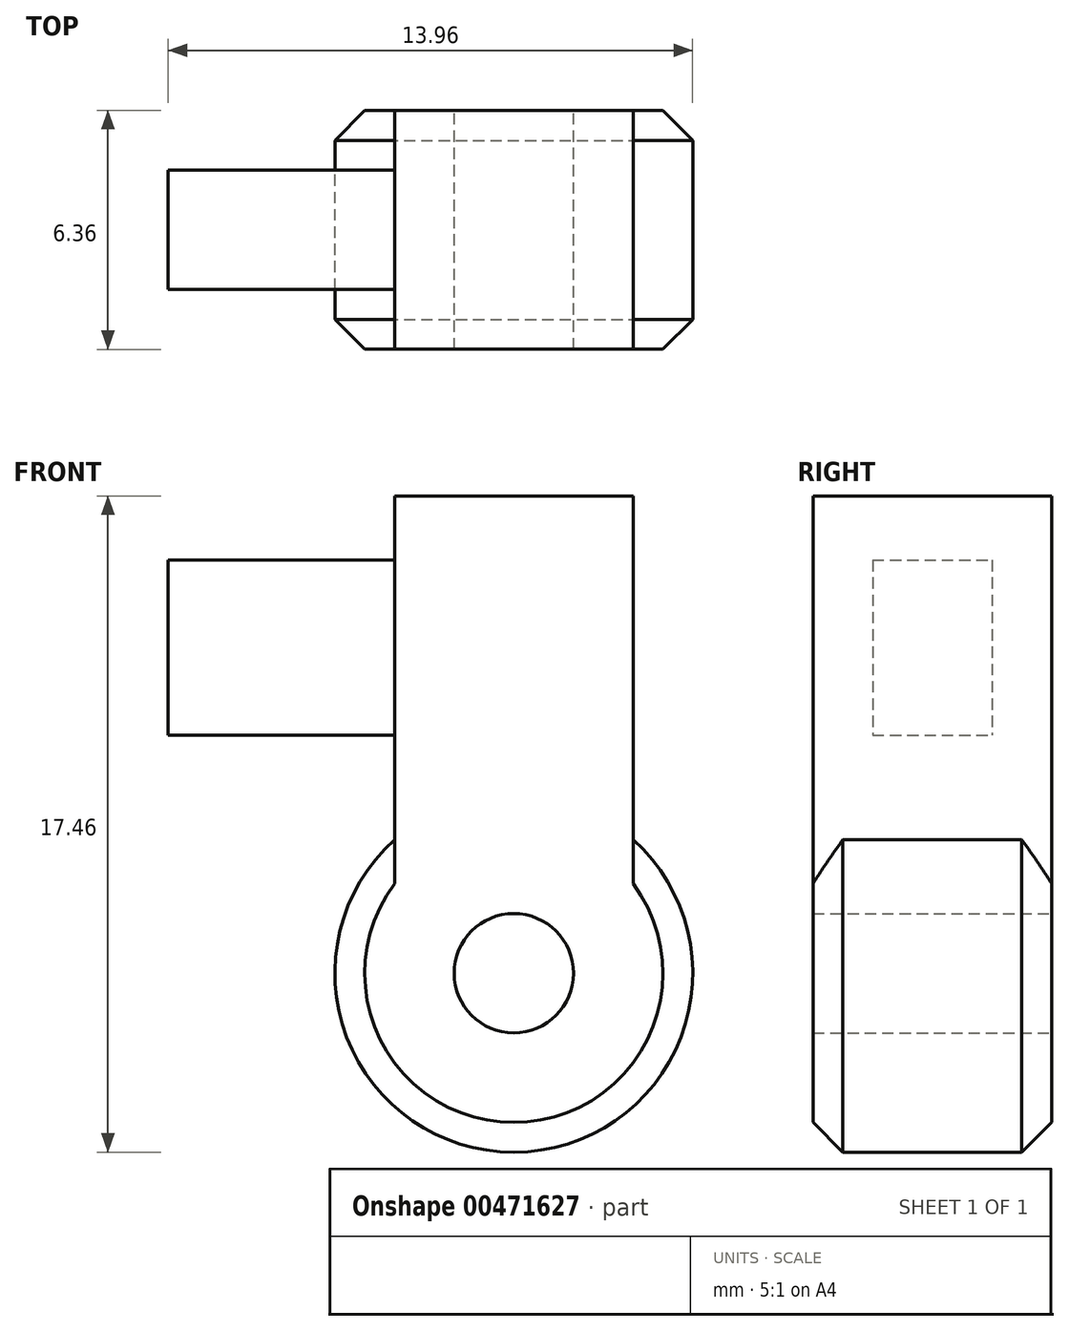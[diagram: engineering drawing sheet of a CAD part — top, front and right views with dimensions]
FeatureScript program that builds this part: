
annotation { "Feature Type Name" : "Feature", "Feature Type Description" : "" }
export const myFeature = defineFeature(function(context is Context, id is Id, definition is map)
    precondition{}
    {
        {
            var Q0;
            Q0=qCreatedBy(makeId("Front.planeOp"),FACE);
            var sketch = newSketch(context, id + "F0", { "sketchPlane" : qUnion([Q0])});
            skLineSegment(sketch, "E0.bottom", {"start": v(77.53, -76.45) * mm, "end": v(-77.53, -76.45) * mm});
            skLineSegment(sketch, "E0.top", {"start": v(77.53, 76.45) * mm, "end": v(-77.53, 76.45) * mm});
            skLineSegment(sketch, "E0.left", {"start": v(77.53, -76.45) * mm, "end": v(77.53, 76.45) * mm});
            skLineSegment(sketch, "E0.right", {"start": v(-77.53, -76.45) * mm, "end": v(-77.53, 76.45) * mm});
            skPoint(sketch, "E0.middle", {"position": v(0, 0) * mm});
            skSolve(sketch);
        }
        {
            var Q0;
            Q0=makeQuery(id+"F0.imprint","IMPRINT",FACE,{"disambiguationData":[TD([[makeQuery(id+"F0.imprint","IMPRINT",EDGE,{"derivedFrom":sQuery(id+"F0.wireOp",EDGE,"E0.bottom")}),-1.0]])]});
            cPlane(context, id + "F1", {"entities" : qUnion([Q0]), "cplaneType" : CPlaneType.OFFSET, "offset" : 25.4 * mm, "width" : 152.4 * mm, "height" : 152.4 * mm});
        }
        {
            var Q0;
            Q0=qCreatedBy(id+"F1.planeOp",FACE);
            var sketch = newSketch(context, id + "F2", { "sketchPlane" : qUnion([Q0])});
            skCircle(sketch, "E1", {"center": v(0, 0) * mm, "radius": 1.59 * mm});
            skCircle(sketch, "E2.0", {"center": v(0, 0) * mm, "radius": 4.76 * mm});
            skSolve(sketch);
        }
        {
            var Q0;
            Q0=qCreatedBy(id+"F1.planeOp",FACE);
            var sketch = newSketch(context, id + "F3", { "sketchPlane" : qUnion([Q0])});
            skLineSegment(sketch, "E3.bottom", {"start": v(3.18, 12.7) * mm, "end": v(-3.18, 12.7) * mm});
            skLineSegment(sketch, "E3.left", {"start": v(3.18, 12.7) * mm, "end": v(3.18, 0) * mm});
            skLineSegment(sketch, "E3.right", {"start": v(-3.18, 12.7) * mm, "end": v(-3.18, 0) * mm});
            skPoint(sketch, "E3.middle", {"position": v(0, 0) * mm});
            skPoint(sketch, "E4", {"position": v(3.18, 0) * mm});
            skPoint(sketch, "E5", {"position": v(-3.18, 0) * mm});
            skLineSegment(sketch, "E6", {"start": v(3.18, 0) * mm, "end": v(-3.18, 0) * mm});
            skCircle(sketch, "E7", {"center": v(0, 0) * mm, "radius": 1.59 * mm});
            skSolve(sketch);
        }
        {
            var Q0;
            Q0=qCreatedBy(id+"F1.planeOp",FACE);
            var sketch = newSketch(context, id + "F4", { "sketchPlane" : qUnion([Q0])});
            skLineSegment(sketch, "E8.bottom", {"start": v(-1.96, 6.34) * mm, "end": v(-9.2, 6.34) * mm});
            skLineSegment(sketch, "E8.top", {"start": v(-1.96, 11) * mm, "end": v(-9.2, 11) * mm});
            skLineSegment(sketch, "E8.left", {"start": v(-1.96, 6.34) * mm, "end": v(-1.96, 11) * mm});
            skLineSegment(sketch, "E8.right", {"start": v(-9.2, 6.34) * mm, "end": v(-9.2, 11) * mm});
            skSolve(sketch);
        }
        {
            var Q0;
            Q0=makeQuery(id+"F2.imprint","IMPRINT",FACE,{"disambiguationData":[TD([[makeQuery(id+"F2.imprint","IMPRINT",EDGE,{"derivedFrom":sQuery(id+"F2.wireOp",EDGE,"E1")}),-1.0]])]});
            extrude(context, id + "F5", {"entities" : qUnion([Q0]), "depth" : 6.35 * mm, "symmetric" : true});
        }
        {
            var Q0;
            Q0=makeQuery(id+"F3.imprint","IMPRINT",FACE,{"disambiguationData":[TD([[makeQuery(id+"F3.imprint","IMPRINT",EDGE,{"derivedFrom":sQuery(id+"F3.wireOp",EDGE,"E3.bottom")}),1.0]])]});
            extrude(context, id + "F6", {"entities" : qUnion([Q0]), "operationType" : NewBodyOperationType.ADD, "depth" : 6.35 * mm, "symmetric" : true});
        }
        {
            var Q0;
            Q0=makeQuery(id+"F4.imprint","IMPRINT",FACE,{"disambiguationData":[TD([[makeQuery(id+"F4.imprint","IMPRINT",EDGE,{"derivedFrom":sQuery(id+"F4.wireOp",EDGE,"E8.bottom")}),-1.0]])]});
            extrude(context, id + "F7", {"entities" : qUnion([Q0]), "operationType" : NewBodyOperationType.ADD, "depth" : 3.17 * mm, "symmetric" : true});
        }
        {
            var Q0;
            Q0=makeQuery(id+"F5.opExtrude","CAP_EDGE",EDGE,{"disambiguationData":[OSD([sQuery(id+"F2.wireOp",EDGE,"E2.0")])],"isStart":false});
            var Q1;
            Q1=makeQuery(id+"F5.opExtrude","CAP_EDGE",EDGE,{"disambiguationData":[OSD([sQuery(id+"F2.wireOp",EDGE,"E2.0")])],"isStart":true});
            chamfer(context, id + "F8", {"entities" : qUnion([Q0, Q1]), "width" : 0.8 * mm, "tangentPropagation" : true});
        }
    });
